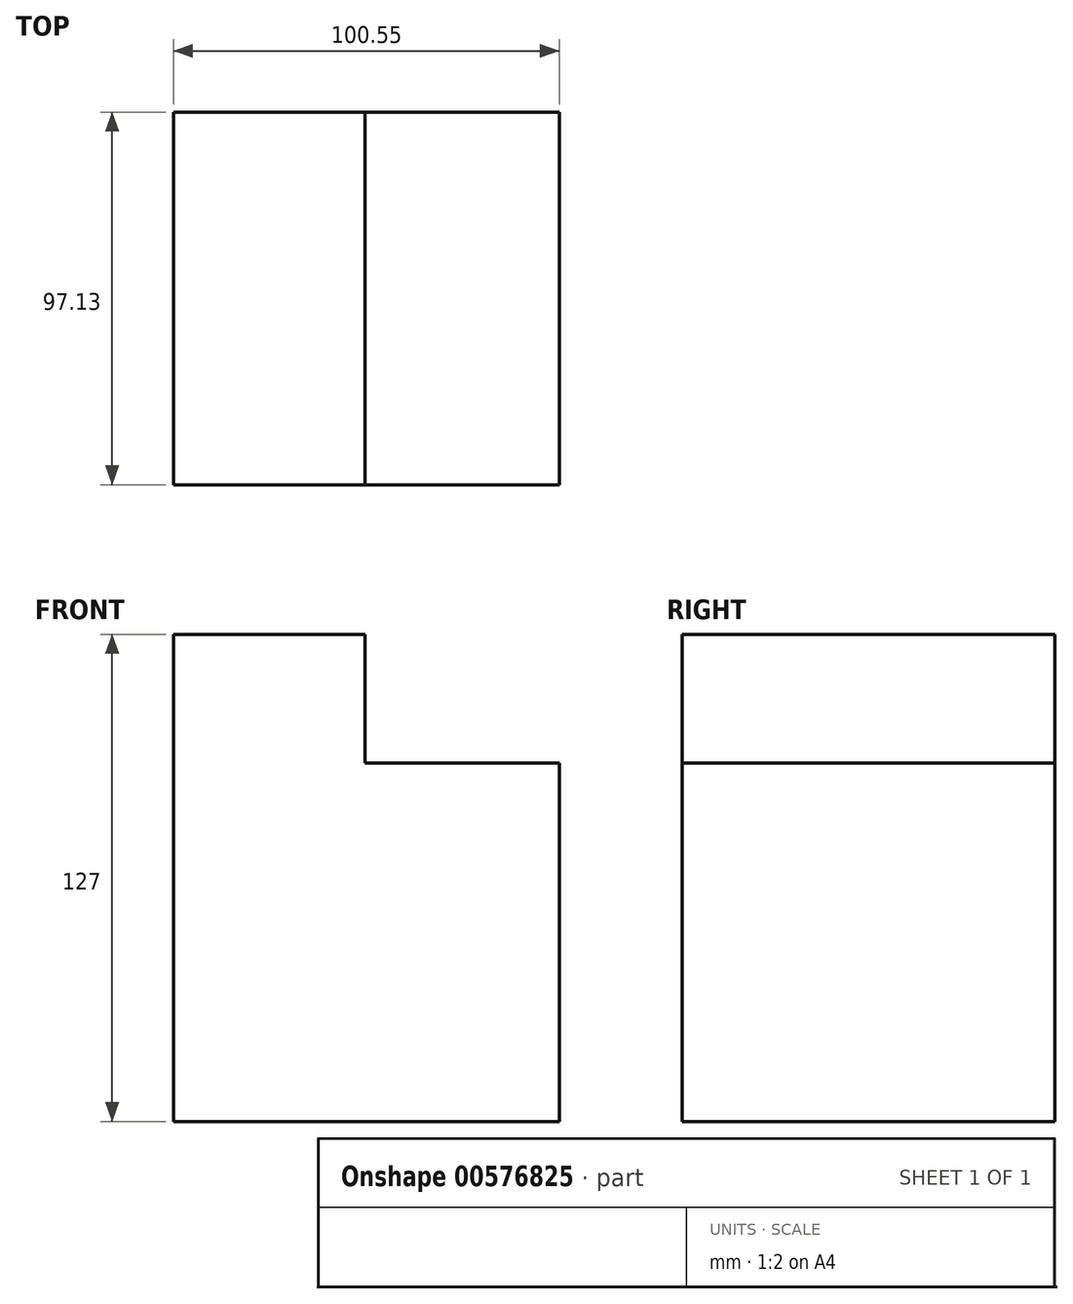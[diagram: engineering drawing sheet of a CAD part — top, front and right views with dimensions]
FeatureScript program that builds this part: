
annotation { "Feature Type Name" : "Feature", "Feature Type Description" : "" }
export const myFeature = defineFeature(function(context is Context, id is Id, definition is map)
    precondition{}
    {
        {
            var Q0;
            Q0=qCreatedBy(makeId("Top.planeOp"),FACE);
            var sketch = newSketch(context, id + "F0", { "sketchPlane" : qUnion([Q0])});
            skLineSegment(sketch, "E0.bottom", {"start": v(-49.92, 0) * mm, "end": v(0, 0) * mm});
            skLineSegment(sketch, "E0.top", {"start": v(-49.92, -71.73) * mm, "end": v(0, -71.73) * mm});
            skLineSegment(sketch, "E0.left", {"start": v(-49.92, 0) * mm, "end": v(-49.92, -71.73) * mm});
            skLineSegment(sketch, "E0.right", {"start": v(0, 0) * mm, "end": v(0, -71.73) * mm});
            skSolve(sketch);
        }
        {
            var Q0;
            Q0 = qSketchRegion(id + "F0", true);
            extrude(context, id + "F1", {"entities" : qUnion([Q0]), "depth" : 127 * mm, "offsetDistance" : 25.4 * mm});
        }
        {
            var Q0;
            Q0=makeQuery(id+"F1.opExtrude","SWEPT_FACE",FACE,{"disambiguationData":[OSD([sQuery(id+"F0.wireOp",EDGE,"E0.right")])]});
            var sketch = newSketch(context, id + "F2", { "sketchPlane" : qUnion([Q0])});
            skLineSegment(sketch, "E1", {"start": v(-71.73, 93.42) * mm, "end": v(0, 93.42) * mm});
            skSolve(sketch);
        }
        {
            var Q0;
            {var subQ0=sQuery(id+"F2.wireOp",EDGE,"E1");Q0=makeQuery(id+"F2.imprint","IMPRINT",FACE,{"disambiguationData":[TD([[makeQuery(id+"F2.imprint","IMPRINT",EDGE,{"derivedFrom":subQ0}),-1.0]])]});}
            extrude(context, id + "F3", {"entities" : qUnion([Q0]), "operationType" : NewBodyOperationType.ADD, "depth" : 50.63 * mm, "offsetDistance" : 25.4 * mm});
        }
        {
            var Q0;
            {var subQ0=sQuery(id+"F0.wireOp",EDGE,"E0.top");Q0=makeQuery(id+"F3.boolean.opBoolean","MERGE",FACE,{"derivedFrom":[makeQuery(id+"F1.opExtrude","SWEPT_FACE",FACE,{"disambiguationData":[OSD([subQ0])]}),makeQuery(id+"F3.opExtrude","SWEPT_FACE",FACE,{"disambiguationData":[OSD([subQ0,sQuery(id+"F0.wireOp",EDGE,"E0.right")])]})]});}
            extrude(context, id + "F4", {"entities" : qUnion([Q0]), "operationType" : NewBodyOperationType.ADD, "depth" : 25.4 * mm, "offsetDistance" : 25.4 * mm});
        }
    });
